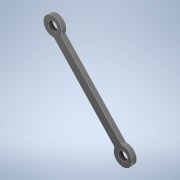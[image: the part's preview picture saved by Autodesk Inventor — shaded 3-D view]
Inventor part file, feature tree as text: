
AUTODESK INVENTOR PART (.ipt)
format: ipt  version: 2022 (Build 260153000, 153)  size: 280,064 bytes
history: native  units: in
note: dims shown in document units (in); Inventor stores cm internally (conversion verified against a paired STEP export)
features: other x1, extrude x1, sketch x1
ambient origin geometry x8: Origin, YZ Plane, XZ Plane, XY Plane, X Axis, Y Axis, Z Axis, Center Point
bodies: Body1 (feature_tree)
feature tree (3):
  other  "Sólido1"
  extrude  "Extrusión1"  Depth=0.0472in
  sketch  "Boceto1"  dims[d7=0.0984in d8=0.1969in d10=0.1969in d11=0.748in d12=0.8268in d14=0.0945in d15=0.0197in d16=0.0472in d17=0.0in]
